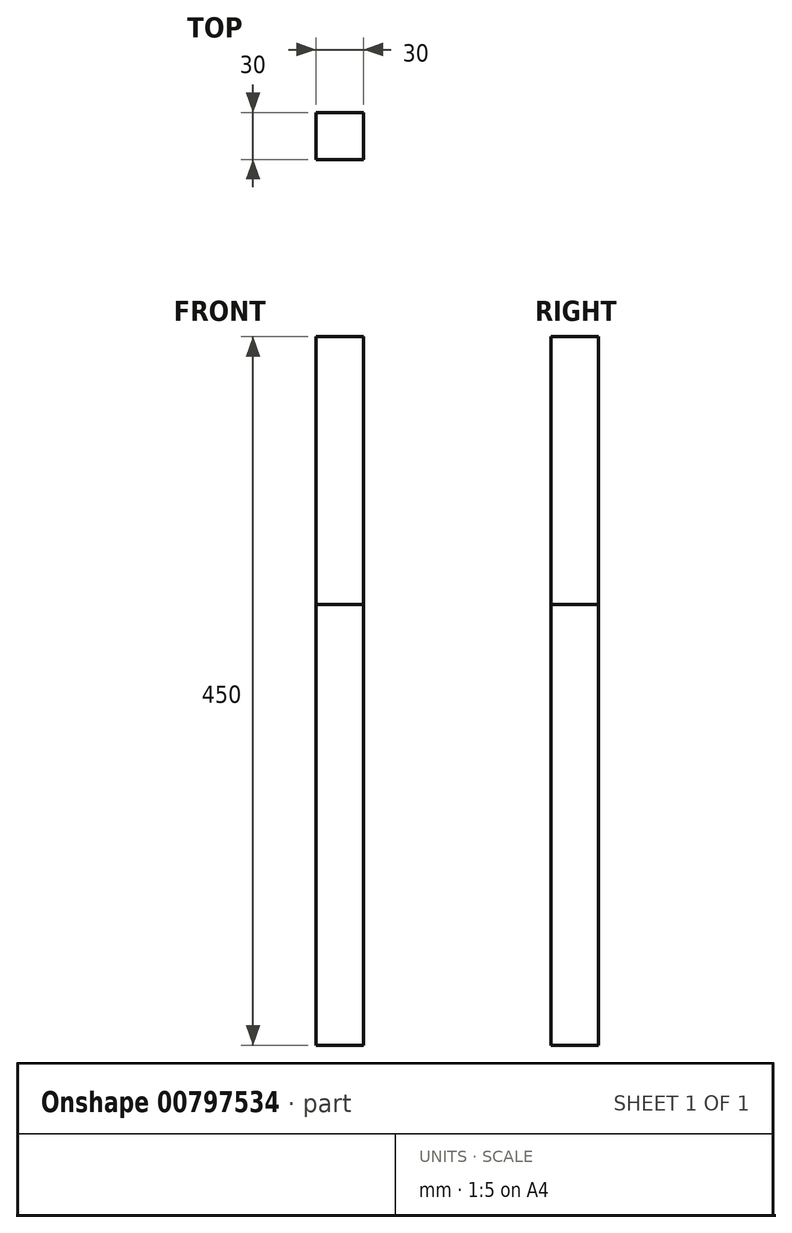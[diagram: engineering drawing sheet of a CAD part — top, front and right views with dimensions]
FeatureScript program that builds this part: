
annotation { "Feature Type Name" : "Feature", "Feature Type Description" : "" }
export const myFeature = defineFeature(function(context is Context, id is Id, definition is map)
    precondition{}
    {
        {
            var Q0;
            Q0=qCreatedBy(makeId("Top.planeOp"),FACE);
            var sketch = newSketch(context, id + "F0", { "sketchPlane" : qUnion([Q0])});
            skLineSegment(sketch, "E0.bottom", {"start": v(15, -15) * mm, "end": v(-15, -15) * mm});
            skLineSegment(sketch, "E0.top", {"start": v(15, 15) * mm, "end": v(-15, 15) * mm});
            skLineSegment(sketch, "E0.left", {"start": v(15, -15) * mm, "end": v(15, 15) * mm});
            skLineSegment(sketch, "E0.right", {"start": v(-15, -15) * mm, "end": v(-15, 15) * mm});
            skPoint(sketch, "E0.middle", {"position": v(0, 0) * mm});
            skSolve(sketch);
        }
        {
            var Q0;
            Q0=makeQuery(id+"F0.imprint","IMPRINT",FACE,{"disambiguationData":[TD([[makeQuery(id+"F0.imprint","IMPRINT",EDGE,{"derivedFrom":sQuery(id+"F0.wireOp",EDGE,"E0.bottom")}),-1.0]])]});
            extrude(context, id + "F1", {"entities" : qUnion([Q0]), "depth" : 450 * mm, "offsetDistance" : 25 * mm});
        }
        {
            var Q0;
            Q0=qCreatedBy(makeId("Top.planeOp"),FACE);
            var sketch = newSketch(context, id + "F2", { "sketchPlane" : qUnion([Q0])});
            skLineSegment(sketch, "E1.bottom", {"start": v(15, -15) * mm, "end": v(-15, -15) * mm});
            skLineSegment(sketch, "E1.top", {"start": v(15, 15) * mm, "end": v(-15, 15) * mm});
            skLineSegment(sketch, "E1.left", {"start": v(15, -15) * mm, "end": v(15, 15) * mm});
            skLineSegment(sketch, "E1.right", {"start": v(-15, -15) * mm, "end": v(-15, 15) * mm});
            skPoint(sketch, "E1.middle", {"position": v(0, 0) * mm});
            skSolve(sketch);
        }
        {
            var Q0;
            Q0 = qSketchRegion(id + "F2", true);
            extrude(context, id + "F3", {"entities" : qUnion([Q0]), "depth" : 280 * mm, "offsetDistance" : 25 * mm});
        }
    });
